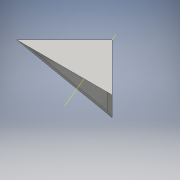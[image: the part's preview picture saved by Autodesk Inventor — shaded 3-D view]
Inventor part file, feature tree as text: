
AUTODESK INVENTOR PART (.ipt)
format: ipt  version: 2016 (Build 200138000, 138)  size: 134,144 bytes
history: native  units: mm
features: sketch x5, other x3, plane x3, extrude x2, projected_geometry x2, pattern_circular x1
ambient origin geometry x8: Origin, YZ Plane, XZ Plane, XY Plane, X Axis, Y Axis, Z Axis, Center Point
bodies: Solid1 (feature_tree)
feature tree (16):
  other  "Table"
  other  "Part2-01"
  extrude  "Extrusion1"  TaperAngle=45.0deg  [1 undecoded]
  sketch  "Sketch4"  dims[d9=82.0mm]
  plane  "Work Plane2"
  sketch  "Sketch5"  dims[d10=3.0mm d11=-7.853982mm d14=30.0mm d15=360.0deg]
  other  "Center Axis"
  pattern_circular  "Circular Pattern1"  Count=3 Angle=360.0deg
  sketch  "Sketch6"  dims[d18=23.671361mm d20=15.0mm]
  plane  "Work Plane4"
  extrude  "Extrusion2"  Depth=15.0mm
  sketch  "Sketch3"  dims[d7=90.0deg d8=45.0deg]
  projected_geometry  "Projected Loop1"
  plane  "Work Plane3"
  sketch  "Sketch7"  dims[d21=3.0mm d22=0.0mm]
  projected_geometry  "Project Cut Edges1"
note: 1 required parameter value undecoded (feature->parameter linkage not recoverable at this tier; creation-order binding heuristic only, values carry confidence <= 0.55)
